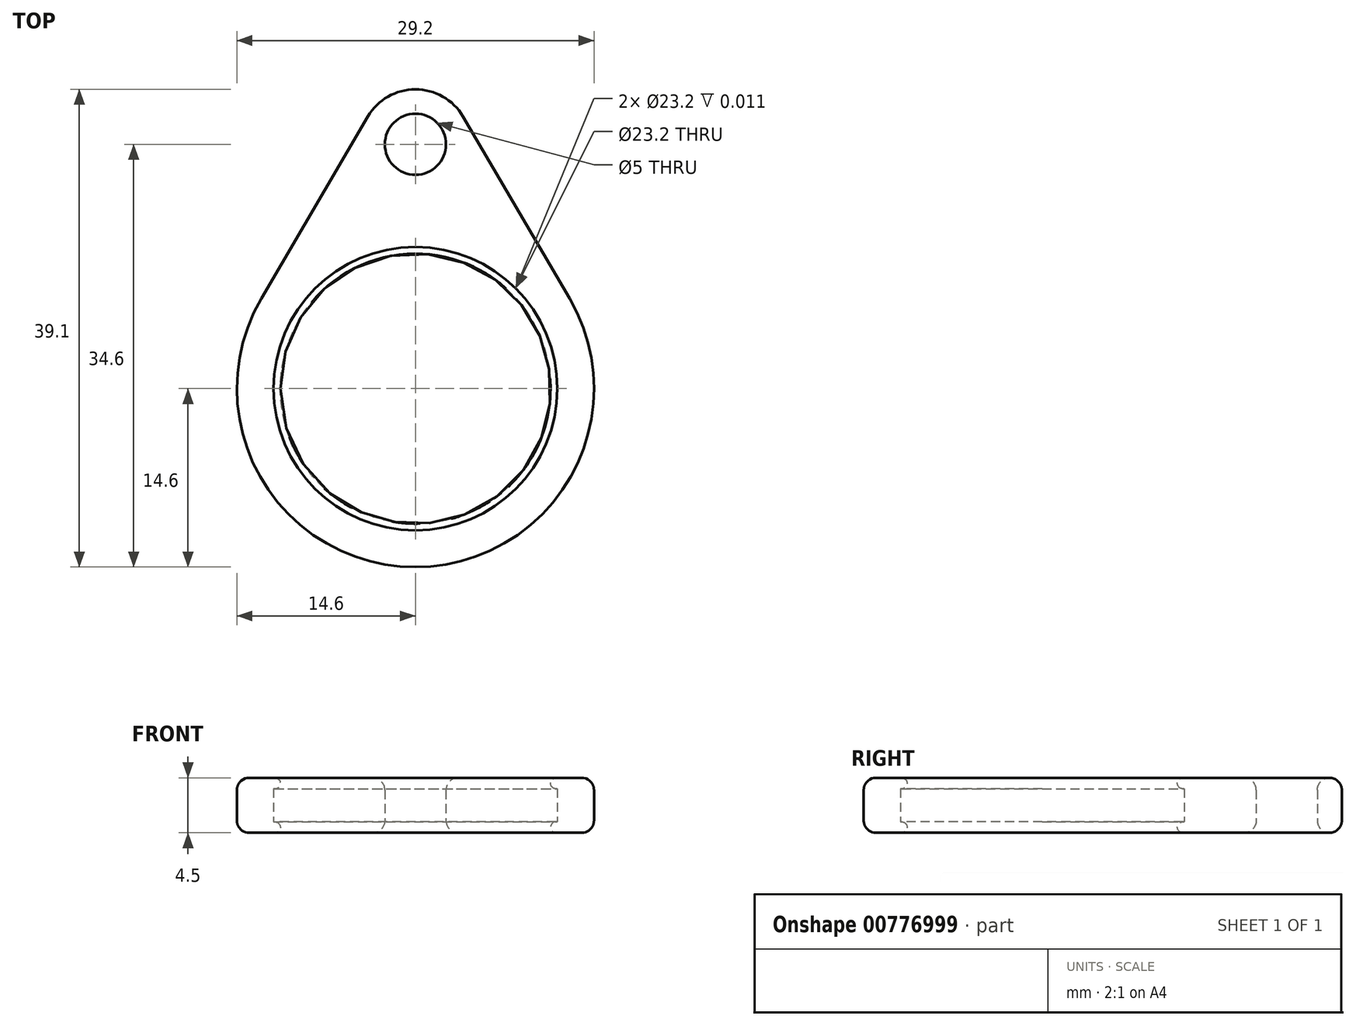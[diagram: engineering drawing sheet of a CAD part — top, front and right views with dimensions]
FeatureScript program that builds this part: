
annotation { "Feature Type Name" : "Feature", "Feature Type Description" : "" }
export const myFeature = defineFeature(function(context is Context, id is Id, definition is map)
    precondition{}
    {
        {
            var Q0;
            Q0=qCreatedBy(makeId("Top.planeOp"),FACE);
            var sketch = newSketch(context, id + "F0", { "sketchPlane" : qUnion([Q0])});
            skCircle(sketch, "E0", {"center": v(0, 0) * mm, "radius": 11.6 * mm});
            skCircle(sketch, "E1", {"center": v(0, 20) * mm, "radius": 2.5 * mm});
            skArc(sketch, "E2", {"start": v(-3.88, 22.27) * mm, "mid": v(0, 24.5) * mm, "end": v(3.88, 22.27) * mm});
            skArc(sketch, "E3", {"start": v(12.6, 7.37) * mm, "mid": v(0, -14.6) * mm, "end": v(-12.6, 7.37) * mm});
            skLineSegment(sketch, "E4", {"start": v(-12.6, 7.37) * mm, "end": v(-3.88, 22.27) * mm});
            skLineSegment(sketch, "E5", {"start": v(3.88, 22.27) * mm, "end": v(12.6, 7.37) * mm});
            skSolve(sketch);
        }
        {
            var Q0;
            Q0 = qSketchRegion(id + "F0", true);
            extrude(context, id + "F1", {"entities" : qUnion([Q0]), "depth" : 4.5 * mm, "offsetDistance" : 25 * mm});
        }
        {
            var Q0;
            Q0=makeQuery(id+"F1.opExtrude","CAP_EDGE",EDGE,{"disambiguationData":[OSD([sQuery(id+"F0.wireOp",EDGE,"E1")])],"isStart":false});
            var Q1;
            Q1=makeQuery(id+"F1.opExtrude","CAP_EDGE",EDGE,{"disambiguationData":[OSD([sQuery(id+"F0.wireOp",EDGE,"E1")])],"isStart":true});
            var Q2;
            Q2=makeQuery(id+"F1.opExtrude","CAP_EDGE",EDGE,{"disambiguationData":[OSD([sQuery(id+"F0.wireOp",EDGE,"E3")])],"isStart":false});
            var Q3;
            Q3=makeQuery(id+"F1.opExtrude","CAP_EDGE",EDGE,{"disambiguationData":[OSD([sQuery(id+"F0.wireOp",EDGE,"E5")])],"isStart":true});
            fillet(context, id + "F2", {"entities" : qUnion([Q0, Q1, Q2, Q3]), "radius" : 1 * mm, "tangentPropagation" : true, "allowEdgeOverflow" : false});
        }
        {
            var Q0;
            Q0=qCreatedBy(makeId("Front.planeOp"),FACE);
            var sketch = newSketch(context, id + "F3", { "sketchPlane" : qUnion([Q0])});
            skLineSegment(sketch, "E6", {"start": v(0, 11.44) * mm, "end": v(0, -4.44) * mm, "construction": true});
            skCircle(sketch, "E7", {"center": v(11.5, 4.05) * mm, "radius": 0.45 * mm});
            skCircle(sketch, "E8", {"center": v(11.5, 0.45) * mm, "radius": 0.45 * mm});
            skSolve(sketch);
        }
        {
            var Q0;
            Q0=makeQuery(id+"F3.imprint","IMPRINT",FACE,{"disambiguationData":[TD([[makeQuery(id+"F3.imprint","IMPRINT",EDGE,{"derivedFrom":sQuery(id+"F3.wireOp",EDGE,"E7")}),1.0]])]});
            var Q1;
            Q1=makeQuery(id+"F3.imprint","IMPRINT",FACE,{"disambiguationData":[TD([[makeQuery(id+"F3.imprint","IMPRINT",EDGE,{"derivedFrom":sQuery(id+"F3.wireOp",EDGE,"E8")}),1.0]])]});
            var Q2;
            Q2=sQuery(id+"F3.wireOp",EDGE,"E6");
            revolve(context, id + "F4", {"operationType" : NewBodyOperationType.ADD, "surfaceOperationType" : NewSurfaceOperationType.NEW, "entities" : qUnion([Q0, Q1]), "axis" : qUnion([Q2]), "revolveType" : RevolveType.FULL});
        }
    });
